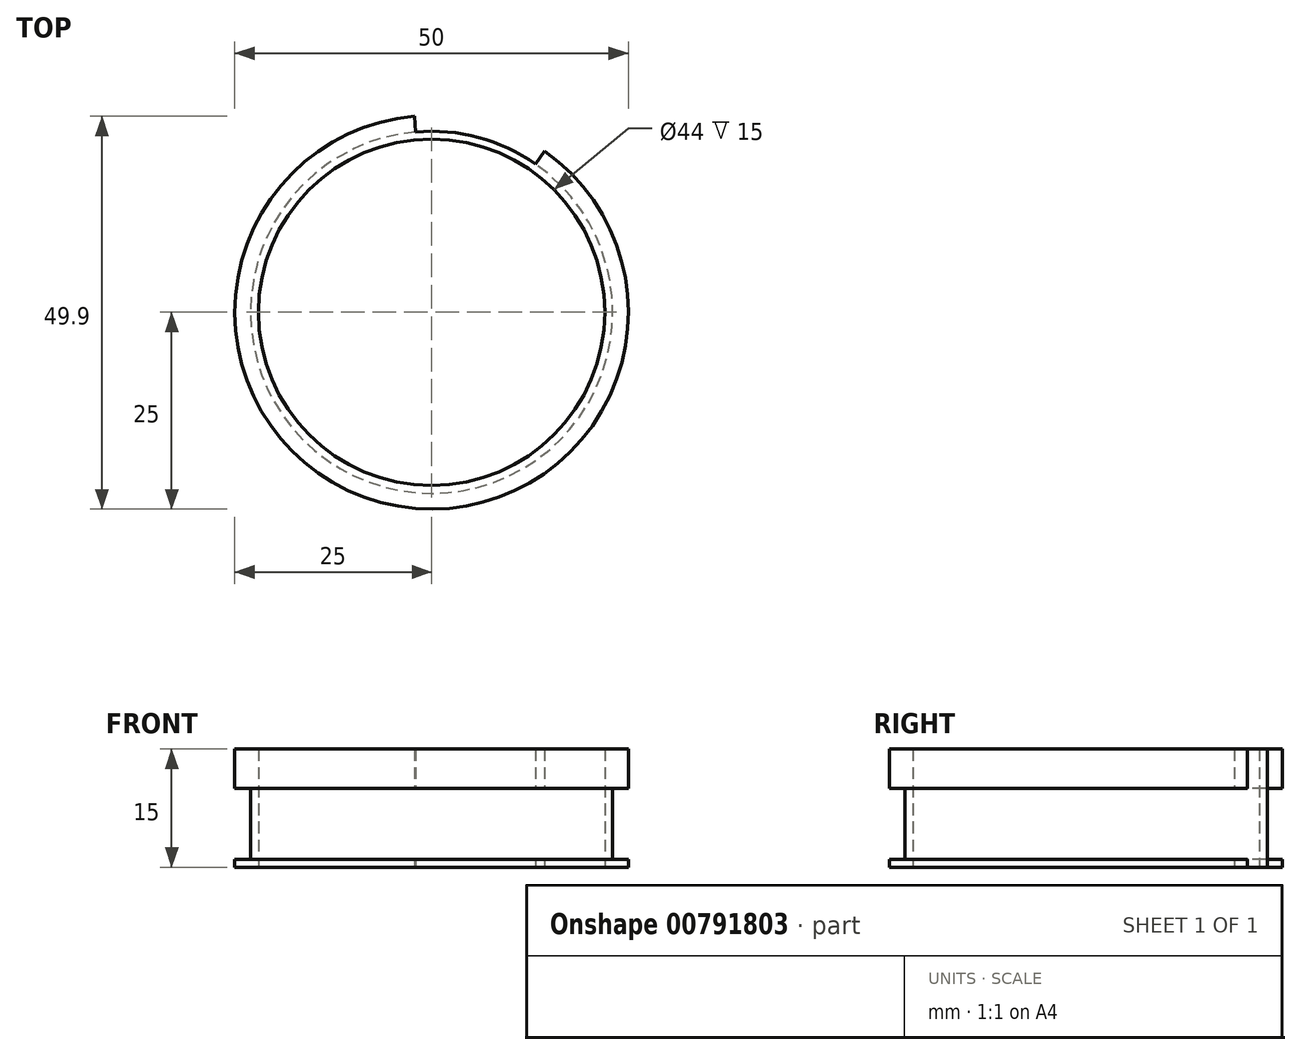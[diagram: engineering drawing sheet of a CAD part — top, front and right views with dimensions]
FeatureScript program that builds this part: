
annotation { "Feature Type Name" : "Feature", "Feature Type Description" : "" }
export const myFeature = defineFeature(function(context is Context, id is Id, definition is map)
    precondition{}
    {
        {
            var Q0;
            Q0=qCreatedBy(makeId("Top.planeOp"),FACE);
            var sketch = newSketch(context, id + "F0", { "sketchPlane" : qUnion([Q0])});
            skCircle(sketch, "E0", {"center": v(0, 0) * mm, "radius": 25 * mm});
            skCircle(sketch, "E1", {"center": v(0, 0) * mm, "radius": 22 * mm});
            skSolve(sketch);
        }
        {
            var Q0;
            Q0 = qSketchRegion(id + "F0", true);
            extrude(context, id + "F1", {"entities" : qUnion([Q0]), "depth" : 15 * mm, "offsetDistance" : 25 * mm});
        }
        {
            var Q0;
            Q0=qCreatedBy(makeId("Top.planeOp"),FACE);
            var sketch = newSketch(context, id + "F2", { "sketchPlane" : qUnion([Q0])});
            skArc(sketch, "E2.0", {"start": v(14.34, 20.48) * mm, "mid": v(6.47, 24.15) * mm, "end": v(-2.18, 24.9) * mm});
            skArc(sketch, "E3", {"start": v(13.2, 18.84) * mm, "mid": v(5.95, 22.22) * mm, "end": v(-2, 22.91) * mm});
            skLineSegment(sketch, "E4", {"start": v(-2, 22.91) * mm, "end": v(-2.18, 24.9) * mm});
            skLineSegment(sketch, "E5", {"start": v(13.2, 18.84) * mm, "end": v(14.34, 20.48) * mm});
            skSolve(sketch);
        }
        {
            var Q0;
            Q0 = qSketchRegion(id + "F2", true);
            var Q1;
            Q1=makeQuery(id+"F1.opExtrude","CAP_FACE",FACE,{"disambiguationData":[OSD([sQuery(id+"F0.wireOp",EDGE,"E0"),sQuery(id+"F0.wireOp",EDGE,"E1")])],"isStart":false});
            extrude(context, id + "F3", {"entities" : qUnion([Q0]), "operationType" : NewBodyOperationType.REMOVE, "endBound" : BoundingType.UP_TO_SURFACE, "depth" : 25 * mm, "endBoundEntityFace" : qUnion([Q1]), "offsetDistance" : 25 * mm});
        }
        {
            var Q0;
            Q0=qCreatedBy(makeId("Top.planeOp"),FACE);
            cPlane(context, id + "F4", {"entities" : qUnion([Q0]), "cplaneType" : CPlaneType.OFFSET, "offset" : 7.5 * mm, "width" : 150 * mm, "height" : 150 * mm});
        }
        {
            var Q0;
            Q0=qCreatedBy(id+"F4.planeOp",FACE);
            var sketch = newSketch(context, id + "F5", { "sketchPlane" : qUnion([Q0])});
            skCircle(sketch, "E6", {"center": v(0, 0) * mm, "radius": 23 * mm});
            skCircle(sketch, "E7", {"center": v(0, 0) * mm, "radius": 38.57 * mm});
            skSolve(sketch);
        }
        {
            var Q0;
            Q0 = qSketchRegion(id + "F5", true);
            extrude(context, id + "F6", {"entities" : qUnion([Q0]), "operationType" : NewBodyOperationType.REMOVE, "endBound" : BoundingType.SYMMETRIC, "oppositeDirection" : true, "depth" : 5 * mm, "offsetDistance" : 25 * mm});
        }
        {
            var Q0;
            {var subQ1=sQuery(id+"F5.wireOp",EDGE,"E6");Q0=makeQuery(id+"F6.boolean.opBoolean","COPY",FACE,{"disambiguationData":[TD([makeQuery(id+"F3.boolean.opBoolean","COPY",FACE,{"derivedFrom":makeQuery(id+"F3.opExtrude","SWEPT_FACE",FACE,{"disambiguationData":[OSD([sQuery(id+"F2.wireOp",EDGE,"E5")])]})})])],"derivedFrom":makeQuery(id+"F6.opExtrude","CAP_FACE",FACE,{"disambiguationData":[OSD([subQ1,sQuery(id+"F5.wireOp",EDGE,"E7")])],"isStart":false})});}
            var sketch = newSketch(context, id + "F7", { "sketchPlane" : qUnion([Q0])});
            skCircle(sketch, "E8", {"center": v(0, 0) * mm, "radius": 23 * mm});
            skCircle(sketch, "E9", {"center": v(0, 0) * mm, "radius": 30.98 * mm});
            skSolve(sketch);
        }
        {
            var Q0;
            Q0 = qSketchRegion(id + "F7", true);
            extrude(context, id + "F8", {"entities" : qUnion([Q0]), "operationType" : NewBodyOperationType.REMOVE, "oppositeDirection" : true, "depth" : 4 * mm, "offsetDistance" : 25 * mm});
        }
    });
